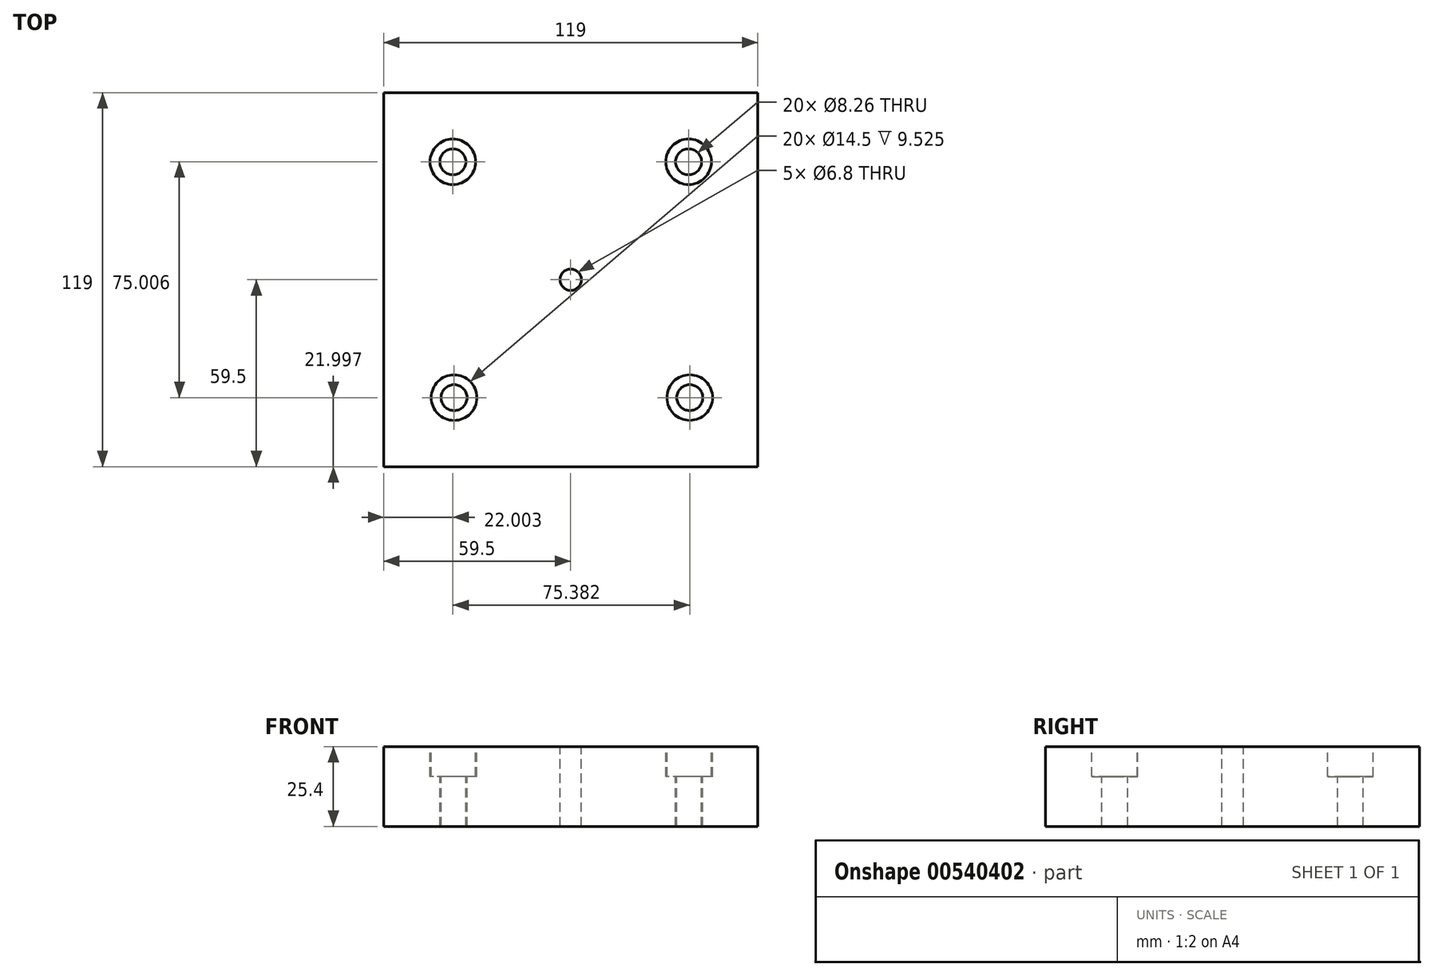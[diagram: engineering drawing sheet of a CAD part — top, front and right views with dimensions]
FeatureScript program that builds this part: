
annotation { "Feature Type Name" : "Feature", "Feature Type Description" : "" }
export const myFeature = defineFeature(function(context is Context, id is Id, definition is map)
    precondition{}
    {
        {
            var Q0;
            Q0=qCreatedBy(makeId("Top.planeOp"),FACE);
            var sketch = newSketch(context, id + "F0", { "sketchPlane" : qUnion([Q0])});
            skLineSegment(sketch, "E0.bottom", {"start": v(-59.5, -59.5) * mm, "end": v(59.5, -59.5) * mm});
            skLineSegment(sketch, "E0.top", {"start": v(-59.5, 59.5) * mm, "end": v(59.5, 59.5) * mm});
            skLineSegment(sketch, "E0.left", {"start": v(-59.5, -59.5) * mm, "end": v(-59.5, 59.5) * mm});
            skLineSegment(sketch, "E0.right", {"start": v(59.5, -59.5) * mm, "end": v(59.5, 59.5) * mm});
            skPoint(sketch, "E0.middle", {"position": v(0, 0) * mm});
            skSolve(sketch);
        }
        {
            var Q0;
            Q0 = qSketchRegion(id + "F0", true);
            extrude(context, id + "F1", {"entities" : qUnion([Q0]), "endBound" : BoundingType.SYMMETRIC, "depth" : 25.4 * mm, "offsetDistance" : 25.4 * mm});
        }
        {
            var Q0;
            Q0=makeQuery(id+"F1.opExtrude","CAP_FACE",FACE,{"disambiguationData":[OSD([sQuery(id+"F0.wireOp",EDGE,"E0.bottom"),sQuery(id+"F0.wireOp",EDGE,"E0.top"),sQuery(id+"F0.wireOp",EDGE,"E0.left"),sQuery(id+"F0.wireOp",EDGE,"E0.right")])],"isStart":false});
            var sketch = newSketch(context, id + "F2", { "sketchPlane" : qUnion([Q0])});
            skCircle(sketch, "E1", {"center": v(37.5, 37.5) * mm, "radius": 5.32 * mm});
            skCircle(sketch, "E2", {"center": v(37.89, -37.5) * mm, "radius": 5.48 * mm});
            skCircle(sketch, "E3", {"center": v(-37.11, -37.5) * mm, "radius": 5.18 * mm});
            skCircle(sketch, "E4", {"center": v(-37.5, 37.5) * mm, "radius": 5.79 * mm});
            skCircle(sketch, "E5", {"center": v(0, 0) * mm, "radius": 8.21 * mm});
            skSolve(sketch);
        }
        {
            var Q0;
            Q0=sQuery(id+"F2.wireOp",VERTEX,"E3.center");
            var Q1;
            Q1=sQuery(id+"F2.wireOp",VERTEX,"E4.center");
            var Q2;
            Q2=sQuery(id+"F2.wireOp",VERTEX,"E1.center");
            var Q3;
            Q3=sQuery(id+"F2.wireOp",VERTEX,"E2.center");
            var Q4;
            Q4=makeQuery(id+"F1.opExtrude","SWEPT_BODY",BODY,{"disambiguationData":[OSD([sQuery(id+"F0.wireOp",EDGE,"E0.bottom"),sQuery(id+"F0.wireOp",EDGE,"E0.top"),sQuery(id+"F0.wireOp",EDGE,"E0.left"),sQuery(id+"F0.wireOp",EDGE,"E0.right")])]});
            hole(context, id + "F3", {"style" : HoleStyle.C_BORE, "endStyle" : HoleEndStyle.THROUGH, "holeDiameter" : 8.25 * mm, "cBoreDiameter" : 14.5 * mm, "cBoreDepth" : 9.52 * mm, "isTappedThrough" : true, "tappedDepth" : 12.7 * mm, "tapClearance" : 3, "locations" : qUnion([Q0, Q1, Q2, Q3]), "scope" : qUnion([Q4])});
        }
        {
            var Q0;
            Q0=makeQuery(id+"F1.opExtrude","CAP_FACE",FACE,{"disambiguationData":[OSD([sQuery(id+"F0.wireOp",EDGE,"E0.bottom"),sQuery(id+"F0.wireOp",EDGE,"E0.top"),sQuery(id+"F0.wireOp",EDGE,"E0.left"),sQuery(id+"F0.wireOp",EDGE,"E0.right")])],"isStart":false});
            var sketch = newSketch(context, id + "F4", { "sketchPlane" : qUnion([Q0])});
            skCircle(sketch, "E6", {"center": v(0, 0) * mm, "radius": 5.36 * mm});
            skSolve(sketch);
        }
        {
            var Q0;
            Q0=sQuery(id+"F4.wireOp",VERTEX,"E6.center");
            var Q1;
            Q1=makeQuery(id+"F1.opExtrude","SWEPT_BODY",BODY,{"disambiguationData":[OSD([sQuery(id+"F0.wireOp",EDGE,"E0.bottom"),sQuery(id+"F0.wireOp",EDGE,"E0.top"),sQuery(id+"F0.wireOp",EDGE,"E0.left"),sQuery(id+"F0.wireOp",EDGE,"E0.right")])]});
            hole(context, id + "F5", {"style" : HoleStyle.SIMPLE, "endStyle" : HoleEndStyle.THROUGH, "standardTappedOrClearance" : lookupTablePath({ "standard" : "ISO", "engagement" : "75%", "pitch" : "1.25 mm", "size" : "M8", "type" : "Tapped" }), "standardBlindInLast" : lookupTablePath({ "standard" : "ISO", "engagement" : "75%", "pitch" : "1.25 mm", "size" : "M8", "type" : "Tapped" }), "holeDiameter" : 6.8 * mm, "showTappedDepth" : true, "isTappedThrough" : true, "tappedDepth" : 19.05 * mm, "tapClearance" : 3, "locations" : qUnion([Q0]), "scope" : qUnion([Q1]), "majorDiameter" : 8 * mm});
        }
    });
